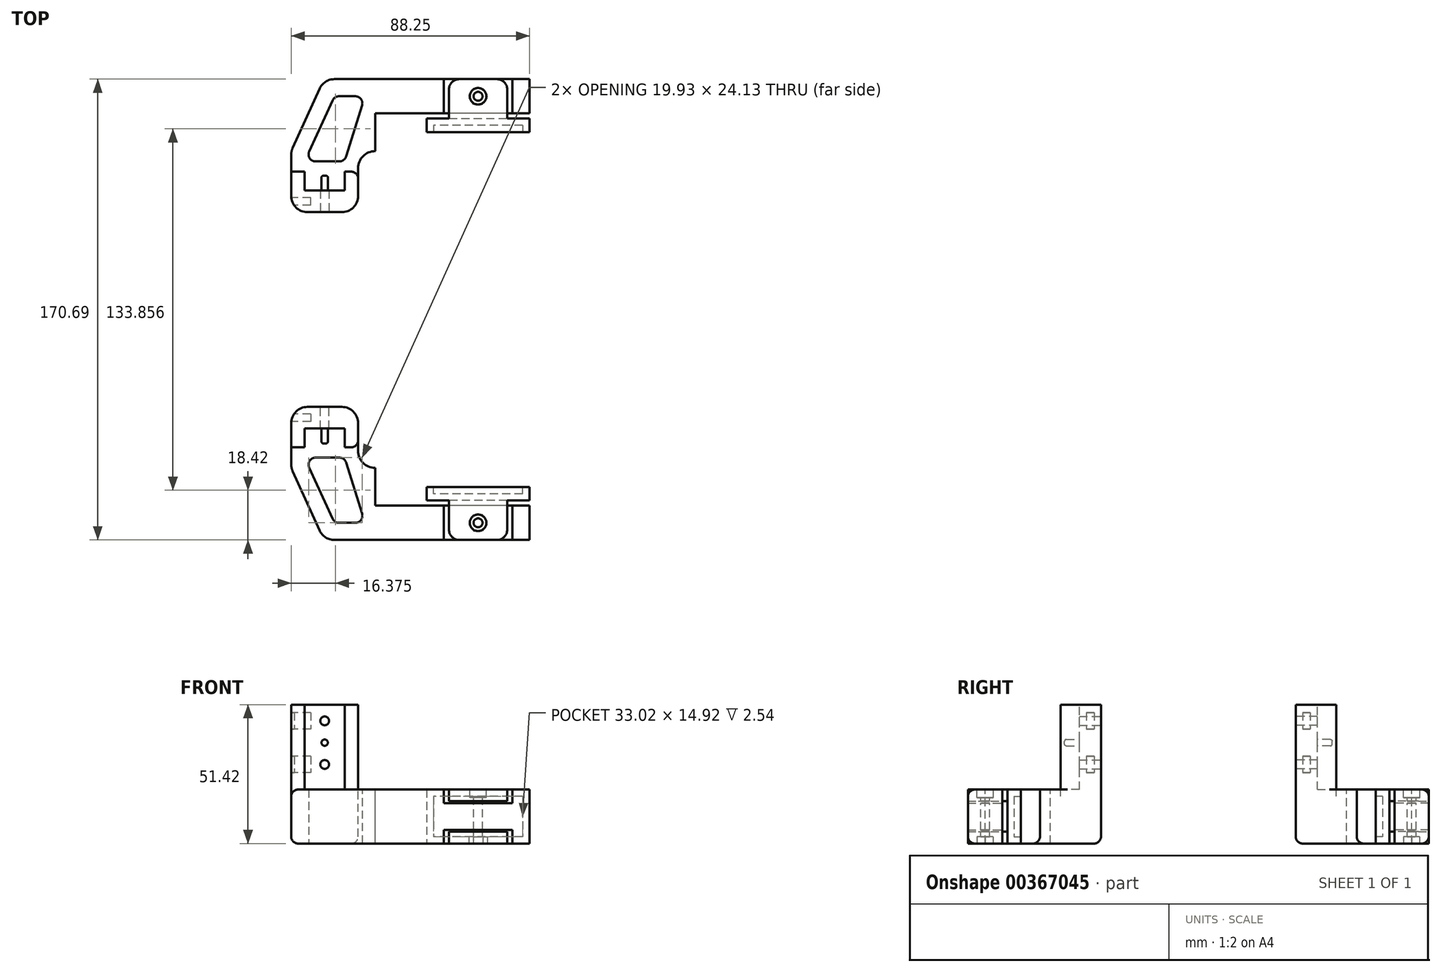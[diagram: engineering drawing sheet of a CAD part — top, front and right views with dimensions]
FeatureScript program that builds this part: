
annotation { "Feature Type Name" : "Feature", "Feature Type Description" : "" }
export const myFeature = defineFeature(function(context is Context, id is Id, definition is map)
    precondition{}
    {
        {
            assignVariable(context, id + "F0", {"name" : "squareNutWidth", "anyValue" : .215});
        }
        {
            var Q0;
            Q0=qCreatedBy(makeId("Front.planeOp"),FACE);
            var sketch = newSketch(context, id + "F1", { "sketchPlane" : qUnion([Q0])});
            skLineSegment(sketch, "E0.bottom", {"start": v(0, 0) * mm, "end": v(-14.75, 0) * mm});
            skLineSegment(sketch, "E0.top", {"start": v(0, 31.42) * mm, "end": v(-14.75, 31.42) * mm});
            skLineSegment(sketch, "E0.left", {"start": v(0, 0) * mm, "end": v(0, 31.42) * mm});
            skLineSegment(sketch, "E0.right", {"start": v(-14.75, 0) * mm, "end": v(-14.75, 31.42) * mm});
            skCircle(sketch, "E1", {"center": v(-7.38, 25.42) * mm, "radius": 1.63 * mm});
            skCircle(sketch, "E2", {"center": v(-7.38, 17.35) * mm, "radius": 1.5 * mm});
            skCircle(sketch, "E3", {"center": v(-7.38, 9.27) * mm, "radius": 1.63 * mm});
            skLineSegment(sketch, "E4", {"start": v(-7.38, 31.42) * mm, "end": v(-7.38, 0) * mm, "construction": true});
            skLineSegment(sketch, "E5", {"start": v(-9, 25.42) * mm, "end": v(-8.88, 17.35) * mm, "construction": true});
            skLineSegment(sketch, "E6", {"start": v(-8.88, 17.35) * mm, "end": v(-9, 9.27) * mm, "construction": true});
            skPoint(sketch, "E7", {"position": v(0, 15.71) * mm});
            skSolve(sketch);
        }
        {
            var Q0;
            Q0=makeQuery(id+"F1.imprint","IMPRINT",FACE,{"disambiguationData":[TD([[makeQuery(id+"F1.imprint","IMPRINT",EDGE,{"derivedFrom":sQuery(id+"F1.wireOp",EDGE,"E0.bottom")}),-1.0]])]});
            var Q1;
            Q1=makeQuery(id+"F1.imprint","IMPRINT",FACE,{"disambiguationData":[TD([[makeQuery(id+"F1.imprint","IMPRINT",EDGE,{"derivedFrom":sQuery(id+"F1.wireOp",EDGE,"E2")}),1.0]])]});
            extrude(context, id + "F2", {"entities" : qUnion([Q0, Q1]), "depth" : 8 * mm, "offsetDistance" : 25.4 * mm});
        }
        {
            var Q0;
            Q0=makeQuery(id+"F2.opExtrude","CAP_FACE",FACE,{"disambiguationData":[OSD([sQuery(id+"F1.wireOp",EDGE,"E0.bottom"),sQuery(id+"F1.wireOp",EDGE,"E0.top"),sQuery(id+"F1.wireOp",EDGE,"E0.left"),sQuery(id+"F1.wireOp",EDGE,"E0.right"),sQuery(id+"F1.wireOp",EDGE,"E1"),sQuery(id+"F1.wireOp",EDGE,"E3")])],"isStart":false});
            var sketch = newSketch(context, id + "F3", { "sketchPlane" : qUnion([Q0])});
            skLineSegment(sketch, "E8", {"start": v(-7.38, 25.42) * mm, "end": v(-7.38, 9.27) * mm, "construction": true});
            skCircle(sketch, "E9", {"center": v(-7.38, 17.35) * mm, "radius": 1.18 * mm});
            skSolve(sketch);
        }
        {
            var Q0;
            Q0=qSketchRegion(id+"F3",true);
            extrude(context, id + "F4", {"entities" : qUnion([Q0]), "operationType" : NewBodyOperationType.ADD, "depth" : 5.5 * mm});
        }
        {
            var Q0;
            Q0=makeQuery(id+"F4.opExtrude","CAP_EDGE",EDGE,{"disambiguationData":[OSD([sQuery(id+"F3.wireOp",EDGE,"E9")])],"isStart":false});
            fillet(context, id + "F5", {"entities" : qUnion([Q0]), "radius" : 0.64 * mm, "tangentPropagation" : true, "allowEdgeOverflow" : false});
        }
        {
            var Q0;
            Q0=makeQuery(id+"F2.opExtrude","SWEPT_FACE",FACE,{"disambiguationData":[OSD([sQuery(id+"F1.wireOp",EDGE,"E0.top")])]});
            var sketch = newSketch(context, id + "F6", { "sketchPlane" : qUnion([Q0])});
            skLineSegment(sketch, "E10.bottom", {"start": v(-14.75, 0) * mm, "end": v(-19.75, 0) * mm});
            skLineSegment(sketch, "E10.top", {"start": v(-14.75, -14.99) * mm, "end": v(-19.75, -14.99) * mm});
            skLineSegment(sketch, "E10.left", {"start": v(-14.75, 0) * mm, "end": v(-14.75, -14.99) * mm});
            skLineSegment(sketch, "E10.right", {"start": v(-19.75, 0) * mm, "end": v(-19.75, -14.99) * mm});
            skLineSegment(sketch, "E11.bottom", {"start": v(0, 0) * mm, "end": v(5, 0) * mm});
            skLineSegment(sketch, "E11.top", {"start": v(0, -14.98) * mm, "end": v(5, -14.98) * mm});
            skLineSegment(sketch, "E11.left", {"start": v(0, 0) * mm, "end": v(0, -14.98) * mm});
            skLineSegment(sketch, "E11.right", {"start": v(5, 0) * mm, "end": v(5, -14.98) * mm});
            skSolve(sketch);
        }
        {
            var Q0;
            Q0=qSketchRegion(id+"F6",true);
            var Q1;
            Q1=makeQuery(id+"F2.opExtrude","SWEPT_FACE",FACE,{"disambiguationData":[OSD([sQuery(id+"F1.wireOp",EDGE,"E0.bottom")])]});
            extrude(context, id + "F7", {"entities" : qUnion([Q0]), "operationType" : NewBodyOperationType.ADD, "endBound" : BoundingType.UP_TO_SURFACE, "oppositeDirection" : true, "depth" : 25.4 * mm, "endBoundEntityFace" : qUnion([Q1]), "offsetDistance" : 25.4 * mm});
        }
        {
            var Q0;
            Q0=makeQuery(id+"F7.opExtrude","SWEPT_FACE",FACE,{"disambiguationData":[OSD([sQuery(id+"F6.wireOp",EDGE,"E10.right")])]});
            var sketch = newSketch(context, id + "F8", { "sketchPlane" : qUnion([Q0])});
            skLineSegment(sketch, "E12", {"start": v(4, 31.42) * mm, "end": v(4, 0) * mm, "construction": true});
            skLineSegment(sketch, "E13.bottom", {"start": v(2.57, 28.5) * mm, "end": v(5.43, 28.5) * mm});
            skLineSegment(sketch, "E13.top", {"start": v(2.57, 22.35) * mm, "end": v(5.43, 22.35) * mm});
            skLineSegment(sketch, "E13.left", {"start": v(2.57, 28.5) * mm, "end": v(2.57, 22.35) * mm});
            skLineSegment(sketch, "E13.right", {"start": v(5.43, 28.5) * mm, "end": v(5.43, 22.35) * mm});
            skLineSegment(sketch, "E14.bottom", {"start": v(2.57, 12.34) * mm, "end": v(5.43, 12.34) * mm});
            skLineSegment(sketch, "E14.top", {"start": v(2.57, 6.2) * mm, "end": v(5.43, 6.2) * mm});
            skLineSegment(sketch, "E14.left", {"start": v(2.57, 12.34) * mm, "end": v(2.57, 6.2) * mm});
            skLineSegment(sketch, "E14.right", {"start": v(5.43, 12.34) * mm, "end": v(5.43, 6.2) * mm});
            skPoint(sketch, "E15", {"position": v(2.57, 25.42) * mm});
            skPoint(sketch, "E16", {"position": v(2.57, 9.27) * mm});
            skPoint(sketch, "E17", {"position": v(4, 12.34) * mm});
            skPoint(sketch, "E18", {"position": v(4, 28.5) * mm});
            skLineSegment(sketch, "E19", {"start": v(0, 31.42) * mm, "end": v(8, 31.42) * mm, "construction": true});
            skSolve(sketch);
        }
        {
            var Q0;
            Q0=qSketchRegion(id+"F8",true);
            extrude(context, id + "F9", {"entities" : qUnion([Q0]), "operationType" : NewBodyOperationType.REMOVE, "oppositeDirection" : true, "depth" : 1.12 / 2 * (getVariable(context, 'squareNutWidth') + 0.56) * mm + 1.12 * 6 * mm, "offsetDistance" : 25.4 * mm});
        }
        {
            var Q0;
            Q0=makeQuery(id+"F2.opExtrude","SWEPT_FACE",FACE,{"disambiguationData":[OSD([sQuery(id+"F1.wireOp",EDGE,"E0.bottom")])]});
            var sketch = newSketch(context, id + "F10", { "sketchPlane" : qUnion([Q0])});
            skLineSegment(sketch, "E20", {"start": v(-7.63, 49.28) * mm, "end": v(68.5, 49.28) * mm});
            skLineSegment(sketch, "E21", {"start": v(68.5, 49.28) * mm, "end": v(68.5, 36.58) * mm});
            skLineSegment(sketch, "E22", {"start": v(68.5, 36.58) * mm, "end": v(11.35, 36.58) * mm});
            skLineSegment(sketch, "E23", {"start": v(-19.75, 14.99) * mm, "end": v(-19.75, 0) * mm});
            skLineSegment(sketch, "E24", {"start": v(-19.75, 0) * mm, "end": v(5, 0) * mm});
            skLineSegment(sketch, "E25", {"start": v(5, 0) * mm, "end": v(5, 14.98) * mm});
            skLineSegment(sketch, "E26", {"start": v(-19.75, 14.99) * mm, "end": v(-19.75, 22.6) * mm});
            skLineSegment(sketch, "E27", {"start": v(-19.75, 22.6) * mm, "end": v(-7.63, 49.28) * mm});
            skLineSegment(sketch, "E28", {"start": v(11.35, 36.58) * mm, "end": v(5, 22.6) * mm});
            skLineSegment(sketch, "E29", {"start": v(5, 22.6) * mm, "end": v(5, 14.98) * mm});
            skLineSegment(sketch, "E30", {"start": v(11.35, 36.58) * mm, "end": v(11.35, 22.6) * mm});
            skLineSegment(sketch, "E31", {"start": v(11.35, 22.6) * mm, "end": v(5, 22.6) * mm});
            skLineSegment(sketch, "E32", {"start": v(-14.75, 18.8) * mm, "end": v(-3.78, 42.93) * mm});
            skLineSegment(sketch, "E33", {"start": v(-3.78, 42.93) * mm, "end": v(7.5, 42.93) * mm});
            skLineSegment(sketch, "E34", {"start": v(0, 18.8) * mm, "end": v(-14.75, 18.8) * mm});
            skLineSegment(sketch, "E35", {"start": v(-14.75, 18.8) * mm, "end": v(-19.75, 18.8) * mm, "construction": true});
            skLineSegment(sketch, "E36", {"start": v(0, 18.8) * mm, "end": v(5, 18.8) * mm, "construction": true});
            skLineSegment(sketch, "E37", {"start": v(-7.63, 49.28) * mm, "end": v(11.35, 36.58) * mm, "construction": true});
            skPoint(sketch, "E38", {"position": v(1.86, 42.93) * mm});
            skLineSegment(sketch, "E39", {"start": v(0, 18.8) * mm, "end": v(7.5, 42.93) * mm});
            skSolve(sketch);
        }
        {
            var Q0;
            Q0=qSketchRegion(id+"F10",true);
            extrude(context, id + "F11", {"entities" : qUnion([Q0]), "operationType" : NewBodyOperationType.ADD, "depth" : 20 * mm, "offsetDistance" : 25.4 * mm});
        }
        {
            var Q0;
            Q0=makeQuery(id+"F11.boolean.opBoolean","MERGE",EDGE,{"derivedFrom":[makeQuery(id+"F7.opExtrude","SWEPT_EDGE",EDGE,{"disambiguationData":[OSD([sQuery(id+"F6.wireOp",EDGE,"E10.bottom"),sQuery(id+"F6.wireOp",EDGE,"E10.right")])]}),makeQuery(id+"F11.opExtrude","SWEPT_EDGE",EDGE,{"disambiguationData":[OSD([sQuery(id+"F10.wireOp",EDGE,"E23"),sQuery(id+"F10.wireOp",EDGE,"E24")])]})]});
            var Q1;
            Q1=makeQuery(id+"F11.boolean.opBoolean","MERGE",EDGE,{"derivedFrom":[makeQuery(id+"F7.opExtrude","SWEPT_EDGE",EDGE,{"disambiguationData":[OSD([sQuery(id+"F6.wireOp",EDGE,"E11.bottom"),sQuery(id+"F6.wireOp",EDGE,"E11.right")])]}),makeQuery(id+"F11.opExtrude","SWEPT_EDGE",EDGE,{"disambiguationData":[OSD([sQuery(id+"F10.wireOp",EDGE,"E24"),sQuery(id+"F10.wireOp",EDGE,"E25")])]})]});
            var Q2;
            Q2=makeQuery(id+"F7.opExtrude","CAP_EDGE",EDGE,{"disambiguationData":[OSD([sQuery(id+"F6.wireOp",EDGE,"E10.top")])],"isStart":false});
            var Q3;
            Q3=makeQuery(id+"F7.opExtrude","CAP_EDGE",EDGE,{"disambiguationData":[OSD([sQuery(id+"F6.wireOp",EDGE,"E11.top")])],"isStart":false});
            var Q4;
            Q4=makeQuery(id+"F11.opExtrude","SWEPT_EDGE",EDGE,{"disambiguationData":[OSD([sQuery(id+"F10.wireOp",EDGE,"E26"),sQuery(id+"F10.wireOp",EDGE,"E27")])]});
            var Q5;
            Q5=makeQuery(id+"F11.opExtrude","SWEPT_EDGE",EDGE,{"disambiguationData":[OSD([sQuery(id+"F10.wireOp",EDGE,"E20"),sQuery(id+"F10.wireOp",EDGE,"E27")])]});
            fillet(context, id + "F12", {"entities" : qUnion([Q0, Q1, Q2, Q3, Q4, Q5]), "radius" : 6 * mm, "tangentPropagation" : true, "allowEdgeOverflow" : false});
        }
        {
            var Q0;
            Q0=makeQuery(id+"F11.opExtrude","SWEPT_EDGE",EDGE,{"disambiguationData":[OSD([sQuery(id+"F10.wireOp",EDGE,"E28"),sQuery(id+"F10.wireOp",EDGE,"E29"),sQuery(id+"F10.wireOp",EDGE,"E31")])]});
            fillet(context, id + "F13", {"entities" : qUnion([Q0]), "radius" : 6.35 * mm, "tangentPropagation" : true, "allowEdgeOverflow" : false});
        }
        {
            var Q0;
            Q0=makeQuery(id+"F11.opExtrude","SWEPT_EDGE",EDGE,{"disambiguationData":[OSD([sQuery(id+"F10.wireOp",EDGE,"E34"),sQuery(id+"F10.wireOp",EDGE,"E39")])]});
            var Q1;
            Q1=makeQuery(id+"F11.opExtrude","SWEPT_EDGE",EDGE,{"disambiguationData":[OSD([sQuery(id+"F10.wireOp",EDGE,"E32"),sQuery(id+"F10.wireOp",EDGE,"E34")])]});
            var Q2;
            Q2=makeQuery(id+"F11.opExtrude","SWEPT_EDGE",EDGE,{"disambiguationData":[OSD([sQuery(id+"F10.wireOp",EDGE,"E33"),sQuery(id+"F10.wireOp",EDGE,"E39")])]});
            var Q3;
            Q3=makeQuery(id+"F11.opExtrude","SWEPT_EDGE",EDGE,{"disambiguationData":[OSD([sQuery(id+"F10.wireOp",EDGE,"E32"),sQuery(id+"F10.wireOp",EDGE,"E33")])]});
            var Q4;
            Q4=makeQuery(id+"F11.opExtrude","CAP_EDGE",EDGE,{"disambiguationData":[OSD([sQuery(id+"F10.wireOp",EDGE,"E20")])],"isStart":true});
            var Q5;
            Q5=makeQuery(id+"F11.opExtrude","CAP_EDGE",EDGE,{"disambiguationData":[OSD([sQuery(id+"F10.wireOp",EDGE,"E20")])],"isStart":false});
            var Q6;
            Q6=makeQuery(id+"F7.opExtrude","SWEPT_EDGE",EDGE,{"disambiguationData":[OSD([sQuery(id+"F6.wireOp",EDGE,"E11.top"),sQuery(id+"F6.wireOp",EDGE,"E11.right")])]});
            fillet(context, id + "F14", {"entities" : qUnion([Q0, Q1, Q2, Q3, Q4, Q5, Q6]), "radius" : 2.54 * mm, "tangentPropagation" : true, "allowEdgeOverflow" : false});
        }
        {
            var Q0;
            Q0=makeQuery(id+"F11.opExtrude","SWEPT_FACE",FACE,{"disambiguationData":[OSD([sQuery(id+"F10.wireOp",EDGE,"E22")])]});
            var sketch = newSketch(context, id + "F15", { "sketchPlane" : qUnion([Q0])});
            skLineSegment(sketch, "E40.bottom", {"start": v(-62.15, 0) * mm, "end": v(-36.75, 0) * mm});
            skLineSegment(sketch, "E40.top", {"start": v(-62.15, -5.08) * mm, "end": v(-36.75, -5.08) * mm});
            skLineSegment(sketch, "E40.left", {"start": v(-62.15, 0) * mm, "end": v(-62.15, -5.08) * mm});
            skLineSegment(sketch, "E40.right", {"start": v(-36.75, 0) * mm, "end": v(-36.75, -5.08) * mm});
            skLineSegment(sketch, "E41.bottom", {"start": v(-62.15, -20) * mm, "end": v(-36.75, -20) * mm});
            skLineSegment(sketch, "E41.top", {"start": v(-62.15, -14.92) * mm, "end": v(-36.75, -14.92) * mm});
            skLineSegment(sketch, "E41.left", {"start": v(-62.15, -20) * mm, "end": v(-62.15, -14.92) * mm});
            skLineSegment(sketch, "E41.right", {"start": v(-36.75, -20) * mm, "end": v(-36.75, -14.92) * mm});
            skLineSegment(sketch, "E42", {"start": v(-62.15, -5.08) * mm, "end": v(-62.15, -14.92) * mm, "construction": true});
            skLineSegment(sketch, "E43", {"start": v(-36.75, -5.08) * mm, "end": v(-36.75, -14.92) * mm, "construction": true});
            skSolve(sketch);
        }
        {
            var Q0;
            Q0=qSketchRegion(id+"F15",true);
            extrude(context, id + "F16", {"entities" : qUnion([Q0]), "operationType" : NewBodyOperationType.REMOVE, "endBound" : BoundingType.THROUGH_ALL, "oppositeDirection" : true, "depth" : 8.9 * mm, "offsetDistance" : 25.4 * mm});
        }
        {
            var Q0;
            Q0=makeQuery(id+"F11.opExtrude","SWEPT_FACE",FACE,{"disambiguationData":[OSD([sQuery(id+"F10.wireOp",EDGE,"E22")])]});
            cPlane(context, id + "F17", {"entities" : qUnion([Q0]), "cplaneType" : CPlaneType.OFFSET, "offset" : 1.9 * mm, "width" : 152.4 * mm, "height" : 152.4 * mm});
        }
        {
            var Q0;
            Q0=qCreatedBy(id+"F17.planeOp",FACE);
            var sketch = newSketch(context, id + "F18", { "sketchPlane" : qUnion([Q0])});
            skLineSegment(sketch, "E44.bottom", {"start": v(-68.5, 0) * mm, "end": v(-30.4, 0) * mm});
            skLineSegment(sketch, "E44.top", {"start": v(-68.5, -20) * mm, "end": v(-30.4, -20) * mm});
            skLineSegment(sketch, "E44.left", {"start": v(-68.5, 0) * mm, "end": v(-68.5, -20) * mm});
            skLineSegment(sketch, "E44.right", {"start": v(-30.4, 0) * mm, "end": v(-30.4, -20) * mm});
            skSolve(sketch);
        }
        {
            var Q0;
            Q0=qSketchRegion(id+"F18",true);
            extrude(context, id + "F19", {"entities" : qUnion([Q0]), "depth" : 5 * mm, "offsetDistance" : 25.4 * mm});
        }
        {
            var Q0;
            Q0=makeQuery(id+"F19.opExtrude","SWEPT_FACE",FACE,{"disambiguationData":[OSD([sQuery(id+"F18.wireOp",EDGE,"E44.left")])]});
            var sketch = newSketch(context, id + "F20", { "sketchPlane" : qUnion([Q0])});
            skLineSegment(sketch, "E45", {"start": v(-29.67, 0) * mm, "end": v(-27.17, -2.5) * mm});
            skLineSegment(sketch, "E46", {"start": v(-27.17, -2.5) * mm, "end": v(-29.67, -5) * mm});
            skLineSegment(sketch, "E47", {"start": v(-29.67, -5) * mm, "end": v(-27.17, -7.5) * mm});
            skLineSegment(sketch, "E48", {"start": v(-27.17, -7.5) * mm, "end": v(-29.67, -10) * mm});
            skLineSegment(sketch, "E49", {"start": v(-29.67, -10) * mm, "end": v(-27.17, -12.5) * mm});
            skLineSegment(sketch, "E50", {"start": v(-27.17, -12.5) * mm, "end": v(-29.67, -15) * mm});
            skLineSegment(sketch, "E51", {"start": v(-29.67, -15) * mm, "end": v(-27.17, -17.5) * mm});
            skLineSegment(sketch, "E52", {"start": v(-27.17, -17.5) * mm, "end": v(-29.67, -20) * mm});
            skLineSegment(sketch, "E53", {"start": v(-29.67, 0) * mm, "end": v(-34.67, 0) * mm});
            skLineSegment(sketch, "E54", {"start": v(-34.67, 0) * mm, "end": v(-34.67, -20) * mm});
            skLineSegment(sketch, "E55", {"start": v(-34.67, -20) * mm, "end": v(-29.67, -20) * mm});
            skSolve(sketch);
        }
        {
            var Q0;
            Q0=makeQuery(id+"F19.opExtrude","CAP_FACE",FACE,{"disambiguationData":[OSD([sQuery(id+"F18.wireOp",EDGE,"E44.bottom"),sQuery(id+"F18.wireOp",EDGE,"E44.top"),sQuery(id+"F18.wireOp",EDGE,"E44.left"),sQuery(id+"F18.wireOp",EDGE,"E44.right")])],"isStart":false});
            var sketch = newSketch(context, id + "F21", { "sketchPlane" : qUnion([Q0])});
            skLineSegment(sketch, "E56.bottom", {"start": v(-65.96, -2.54) * mm, "end": v(-32.94, -2.54) * mm});
            skLineSegment(sketch, "E56.top", {"start": v(-65.96, -17.46) * mm, "end": v(-32.94, -17.46) * mm});
            skLineSegment(sketch, "E56.left", {"start": v(-65.96, -2.54) * mm, "end": v(-65.96, -17.46) * mm});
            skLineSegment(sketch, "E56.right", {"start": v(-32.94, -2.54) * mm, "end": v(-32.94, -17.46) * mm});
            skLineSegment(sketch, "E57", {"start": v(-49.45, 0) * mm, "end": v(-49.45, -2.54) * mm, "construction": true});
            skLineSegment(sketch, "E58", {"start": v(-30.4, -10) * mm, "end": v(-32.94, -10) * mm, "construction": true});
            skSolve(sketch);
        }
        {
            var Q0;
            Q0=qSketchRegion(id+"F21",true);
            extrude(context, id + "F22", {"entities" : qUnion([Q0]), "operationType" : NewBodyOperationType.REMOVE, "oppositeDirection" : true, "depth" : 2.54 * mm, "offsetDistance" : 25.4 * mm});
        }
        {
            var Q0;
            Q0=makeQuery(id+"F19.opExtrude","CAP_FACE",FACE,{"disambiguationData":[OSD([sQuery(id+"F18.wireOp",EDGE,"E44.bottom"),sQuery(id+"F18.wireOp",EDGE,"E44.top"),sQuery(id+"F18.wireOp",EDGE,"E44.left"),sQuery(id+"F18.wireOp",EDGE,"E44.right")])],"isStart":true});
            var sketch = newSketch(context, id + "F23", { "sketchPlane" : qUnion([Q0])});
            skLineSegment(sketch, "E59.bottom", {"start": v(38.66, 0) * mm, "end": v(60.25, 0) * mm});
            skLineSegment(sketch, "E59.top", {"start": v(38.66, -4.36) * mm, "end": v(60.25, -4.36) * mm});
            skLineSegment(sketch, "E59.left", {"start": v(38.66, 0) * mm, "end": v(38.66, -4.36) * mm});
            skLineSegment(sketch, "E59.right", {"start": v(60.25, 0) * mm, "end": v(60.25, -4.36) * mm});
            skLineSegment(sketch, "E60.bottom", {"start": v(60.25, -20) * mm, "end": v(38.66, -20) * mm});
            skLineSegment(sketch, "E60.top", {"start": v(60.25, -15.64) * mm, "end": v(38.66, -15.64) * mm});
            skLineSegment(sketch, "E60.left", {"start": v(60.25, -20) * mm, "end": v(60.25, -15.64) * mm});
            skLineSegment(sketch, "E60.right", {"start": v(38.66, -20) * mm, "end": v(38.66, -15.64) * mm});
            skPoint(sketch, "E61", {"position": v(49.45, 0) * mm});
            skPoint(sketch, "E62", {"position": v(49.45, -4.36) * mm});
            skSolve(sketch);
        }
        {
            var Q0;
            Q0=qSketchRegion(id+"F23",true);
            var Q1;
            Q1=makeQuery(id+"F11.opExtrude","SWEPT_FACE",FACE,{"disambiguationData":[OSD([sQuery(id+"F10.wireOp",EDGE,"E20")])]});
            extrude(context, id + "F24", {"entities" : qUnion([Q0]), "operationType" : NewBodyOperationType.ADD, "endBound" : BoundingType.UP_TO_SURFACE, "depth" : 9.27 * mm, "endBoundEntityFace" : qUnion([Q1]), "offsetDistance" : 25.4 * mm});
        }
        {
            var Q0;
            Q0=makeQuery(id+"F24.boolean.opBoolean","MERGE",FACE,{"derivedFrom":[makeQuery(id+"F19.opExtrude","SWEPT_FACE",FACE,{"disambiguationData":[OSD([sQuery(id+"F18.wireOp",EDGE,"E44.bottom")])]}),makeQuery(id+"F24.opExtrude","SWEPT_FACE",FACE,{"disambiguationData":[OSD([sQuery(id+"F23.wireOp",EDGE,"E59.bottom")])]})]});
            var sketch = newSketch(context, id + "F25", { "sketchPlane" : qUnion([Q0])});
            skCircle(sketch, "E63", {"center": v(49.45, -42.93) * mm, "radius": 1.66 * mm});
            skLineSegment(sketch, "E64", {"start": v(49.45, -36.58) * mm, "end": v(49.45, -49.28) * mm, "construction": true});
            skSolve(sketch);
        }
        {
            var Q0;
            Q0=qSketchRegion(id+"F25",true);
            extrude(context, id + "F26", {"entities" : qUnion([Q0]), "operationType" : NewBodyOperationType.REMOVE, "endBound" : BoundingType.THROUGH_ALL, "oppositeDirection" : true, "depth" : 25.4 * mm, "offsetDistance" : 25.4 * mm});
        }
        {
            var Q0;
            Q0=makeQuery(id+"F24.boolean.opBoolean","MERGE",FACE,{"derivedFrom":[makeQuery(id+"F19.opExtrude","SWEPT_FACE",FACE,{"disambiguationData":[OSD([sQuery(id+"F18.wireOp",EDGE,"E44.bottom")])]}),makeQuery(id+"F24.opExtrude","SWEPT_FACE",FACE,{"disambiguationData":[OSD([sQuery(id+"F23.wireOp",EDGE,"E59.bottom")])]})]});
            var sketch = newSketch(context, id + "F27", { "sketchPlane" : qUnion([Q0])});
            skCircle(sketch, "E65", {"center": v(49.45, -42.93) * mm, "radius": 3.07 * mm});
            skSolve(sketch);
        }
        {
            var Q0;
            Q0=qSketchRegion(id+"F27",true);
            extrude(context, id + "F28", {"entities" : qUnion([Q0]), "operationType" : NewBodyOperationType.REMOVE, "oppositeDirection" : true, "depth" : 3 * mm, "offsetDistance" : 25.4 * mm});
        }
        {
            var Q0;
            Q0=makeQuery(id+"F24.boolean.opBoolean","MERGE",FACE,{"derivedFrom":[makeQuery(id+"F19.opExtrude","SWEPT_FACE",FACE,{"disambiguationData":[OSD([sQuery(id+"F18.wireOp",EDGE,"E44.top")])]}),makeQuery(id+"F24.opExtrude","SWEPT_FACE",FACE,{"disambiguationData":[OSD([sQuery(id+"F23.wireOp",EDGE,"E60.bottom")])]})]});
            var sketch = newSketch(context, id + "F29", { "sketchPlane" : qUnion([Q0])});
            skCircle(sketch, "E66.cCircle", {"center": v(49.45, 42.93) * mm, "radius": 3.01 * mm, "construction": true});
            skLineSegment(sketch, "E66.0", {"start": v(47.7, 45.94) * mm, "end": v(51.2, 45.94) * mm});
            skLineSegment(sketch, "E66.1", {"start": v(51.2, 45.94) * mm, "end": v(52.93, 42.93) * mm});
            skLineSegment(sketch, "E66.2", {"start": v(52.93, 42.93) * mm, "end": v(51.2, 39.91) * mm});
            skLineSegment(sketch, "E66.3", {"start": v(51.2, 39.91) * mm, "end": v(47.7, 39.91) * mm});
            skLineSegment(sketch, "E66.4", {"start": v(47.7, 39.91) * mm, "end": v(45.97, 42.93) * mm});
            skLineSegment(sketch, "E66.5", {"start": v(45.97, 42.93) * mm, "end": v(47.7, 45.94) * mm});
            skPoint(sketch, "E66.0.midPoint", {"position": v(49.45, 45.94) * mm});
            skSolve(sketch);
        }
        {
            var Q0;
            Q0=qSketchRegion(id+"F29",true);
            extrude(context, id + "F30", {"entities" : qUnion([Q0]), "operationType" : NewBodyOperationType.REMOVE, "oppositeDirection" : true, "depth" : 2.5 * mm, "offsetDistance" : 25.4 * mm});
        }
        {
            var Q0;
            Q0=makeQuery(id+"F24.opExtrude","CAP_EDGE",EDGE,{"disambiguationData":[OSD([sQuery(id+"F23.wireOp",EDGE,"E59.left")])],"isStart":false});
            var Q1;
            Q1=makeQuery(id+"F24.opExtrude","CAP_EDGE",EDGE,{"disambiguationData":[OSD([sQuery(id+"F23.wireOp",EDGE,"E59.right")])],"isStart":false});
            var Q2;
            Q2=makeQuery(id+"F24.opExtrude","CAP_EDGE",EDGE,{"disambiguationData":[OSD([sQuery(id+"F23.wireOp",EDGE,"E60.left")])],"isStart":false});
            var Q3;
            Q3=makeQuery(id+"F24.opExtrude","CAP_EDGE",EDGE,{"disambiguationData":[OSD([sQuery(id+"F23.wireOp",EDGE,"E60.right")])],"isStart":false});
            var Q4;
            Q4=makeQuery(id+"F16.boolean.opBoolean","COPY",EDGE,{"derivedFrom":makeQuery(id+"F16.opExtrude","CAP_EDGE",EDGE,{"disambiguationData":[OSD([sQuery(id+"F15.wireOp",EDGE,"E40.left")])],"isStart":true})});
            var Q5;
            Q5=makeQuery(id+"F16.boolean.opBoolean","COPY",EDGE,{"derivedFrom":makeQuery(id+"F16.opExtrude","CAP_EDGE",EDGE,{"disambiguationData":[OSD([sQuery(id+"F15.wireOp",EDGE,"E40.right")])],"isStart":true})});
            var Q6;
            Q6=makeQuery(id+"F16.boolean.opBoolean","COPY",EDGE,{"derivedFrom":makeQuery(id+"F16.opExtrude","CAP_EDGE",EDGE,{"disambiguationData":[OSD([sQuery(id+"F15.wireOp",EDGE,"E41.left")])],"isStart":true})});
            var Q7;
            Q7=makeQuery(id+"F16.boolean.opBoolean","COPY",EDGE,{"derivedFrom":makeQuery(id+"F16.opExtrude","CAP_EDGE",EDGE,{"disambiguationData":[OSD([sQuery(id+"F15.wireOp",EDGE,"E41.right")])],"isStart":true})});
            fillet(context, id + "F31", {"entities" : qUnion([Q0, Q1, Q2, Q3, Q4, Q5, Q6, Q7]), "radius" : 3.8 * mm, "tangentPropagation" : true, "allowEdgeOverflow" : false});
        }
        {
            var Q0;
            Q0=qCreatedBy(makeId("Front.planeOp"),FACE);
            cPlane(context, id + "F32", {"entities" : qUnion([Q0]), "cplaneType" : CPlaneType.OFFSET, "offset" : 36.07 * mm, "oppositeDirection" : true, "width" : 152.4 * mm, "height" : 152.4 * mm});
        }
        {
            var Q0;
            Q0=makeQuery(id+"F2.opExtrude","SWEPT_BODY",BODY,{"disambiguationData":[OSD([sQuery(id+"F1.wireOp",EDGE,"E0.bottom"),sQuery(id+"F1.wireOp",EDGE,"E0.top"),sQuery(id+"F1.wireOp",EDGE,"E0.left"),sQuery(id+"F1.wireOp",EDGE,"E0.right"),sQuery(id+"F1.wireOp",EDGE,"E1"),sQuery(id+"F1.wireOp",EDGE,"E3")])]});
            var Q1;
            Q1=makeQuery(id+"F19.opExtrude","SWEPT_BODY",BODY,{"disambiguationData":[OSD([sQuery(id+"F18.wireOp",EDGE,"E44.bottom"),sQuery(id+"F18.wireOp",EDGE,"E44.top"),sQuery(id+"F18.wireOp",EDGE,"E44.left"),sQuery(id+"F18.wireOp",EDGE,"E44.right")])]});
            var Q2;
            Q2=qCreatedBy(id+"F32.planeOp",FACE);
            mirror(context, id + "F33", {"entities" : qUnion([Q0, Q1]), "mirrorPlane" : qUnion([Q2])});
        }
    });
